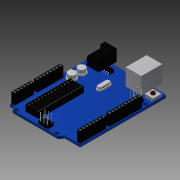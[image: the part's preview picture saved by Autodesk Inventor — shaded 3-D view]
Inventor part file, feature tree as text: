
AUTODESK INVENTOR PART (.ipt)
format: ipt  version: 2014 SP1 (Build 180222100, 222)  size: 1,044,992 bytes
history: native  units: mm
features: sketch x31, extrude x29, pattern_linear x9, revolve x5, fillet x2, plane x1, mirror x1
ambient origin geometry x8: Origin, YZ Plane, XZ Plane, XY Plane, X Axis, Y Axis, Z Axis, Center Point
bodies: Solid1 (feature_tree)
feature tree (78):
  extrude  "Extrusion1"  Depth=69.0mm
  extrude  "Extrusion2"  Depth=3.0mm
  sketch  "Sketch4"  dims[d10=3.0mm d11=5.0mm]
  extrude  "Extrusion3"  Depth=5.0mm
  pattern_linear  "Rectangular Pattern1"  Count1=6 Spacing1=2.5mm
  extrude  "Extrusion4"  Depth=2.5mm
  pattern_linear  "Rectangular Pattern2"  Count1=8 Spacing1=2.5mm
  sketch  "Sketch5"  dims[d13=3.0mm]
  extrude  "Extrusion5"  Depth=2.5mm
  pattern_linear  "Rectangular Pattern3"  Count1=8 Spacing1=2.5mm
  extrude  "Extrusion6"  Depth=2.5mm
  pattern_linear  "Rectangular Pattern4"  Count1=10 Spacing1=2.5mm
  sketch  "Sketch6"  dims[d15=21.587978mm]
  extrude  "Extrusion7"  Depth=35.0mm
  pattern_linear  "Rectangular Pattern5"  Spacing1=1.5mm  [1 undecoded]
  extrude  "Extrusion10"  Depth=2.5mm
  extrude  "Extrusion11"  Depth=1.25mm
  extrude  "Extrusion12"  Depth=1.5mm
  fillet  "Fillet1"  Radius=0.5mm
  extrude  "Extrusion13"  Depth=4.0mm TaperAngle=0.0deg
  pattern_linear  "Rectangular Pattern6"  Count1=14 Spacing1=2.5mm
  extrude  "Extrusion14"  Depth=4.0mm TaperAngle=0.0deg
  extrude  "Extrusion15"  Depth=1.0mm TaperAngle=0.0deg
  extrude  "Extrusion16"  Depth=2.5mm
  extrude  "Extrusion17"  Depth=5.0mm
  extrude  "Extrusion18"  Depth=0.5mm
  extrude  "Extrusion19"  Depth=24.0mm
  revolve  "Revolution1"  [1 undecoded]
  pattern_linear  "Rectangular Pattern7"  Spacing1=0.5mm  [1 undecoded]
  plane  "Work Plane1"
  mirror  "Mirror1"
  extrude  "Extrusion20"  Depth=0.5mm
  sketch  "Sketch21"  dims[d33=8.0mm d34=0.0mm d35=80.0mm d37=2.5mm]
  sketch  "Sketch22"  dims[d38=2.5mm d39=2.5mm]
  extrude  "Extrusion21"  Depth=0.5mm
  extrude  "Extrusion22"  Depth=3.5mm
  extrude  "Extrusion23"  Depth=2.0mm TaperAngle=0.0deg
  revolve  "Revolution2"  [1 undecoded]
  pattern_linear  "Rectangular Pattern8"  Spacing1=3.0mm  [1 undecoded]
  revolve  "Revolution3"  [1 undecoded]
  extrude  "Extrusion24"  Depth=2.5mm
  extrude  "Extrusion25"  Depth=3.0mm
  extrude  "Extrusion26"  Depth=2.0mm TaperAngle=0.0deg
  extrude  "Extrusion27"  Depth=13.999995mm
  revolve  "Revolution4"  [1 undecoded]
  revolve  "Revolution5"  [1 undecoded]
  extrude  "Extrusion28"  Depth=14.0mm
  extrude  "Extrusion29"  Depth=2.0mm
  extrude  "Extrusion30"  Depth=3.0mm
  fillet  "Fillet2"  Radius=14.0mm
  extrude  "Extrusion31"  Depth=2.0mm
  pattern_linear  "Rectangular Pattern9"  Spacing1=2.0mm  [1 undecoded]
  sketch  "Sketch1"  dims[d0=54.0mm d1=69.0mm]
  sketch  "Sketch3"  dims[d2=2.0mm d3=0.0mm d9=3.0mm]
  sketch  "Sketch9"  dims[d16=2.0mm d17=0.0mm]
  sketch  "Sketch10"  dims[d18=2.5mm]
  sketch  "Sketch11"  dims[d19=2.5mm]
  sketch  "Sketch12"  dims[d20=1.5mm]
  sketch  "Sketch13"  dims[d21=0.5mm]
  sketch  "Sketch14"  dims[d22=0.5mm]
  sketch  "Sketch15"  dims[d23=8.0mm d24=0.0mm d25=60.0mm d27=2.5mm]
  sketch  "Sketch16"  dims[d28=2.5mm d29=2.5mm]
  sketch  "Sketch17"  dims[d30=0.5mm]
  sketch  "Sketch19"  dims[d31=1.5mm]
  sketch  "Sketch20"  dims[d32=17.5mm]
  sketch  "Sketch23"  dims[d40=0.5mm]
  sketch  "Sketch24"  dims[d41=0.5mm]
  sketch  "Sketch25"  dims[d42=1.5mm]
  sketch  "Sketch26"  dims[d43=8.0mm d44=0.0mm d45=80.0mm d47=2.5mm]
  sketch  "Sketch27"  dims[d48=2.5mm d49=2.5mm]
  sketch  "Sketch28"  dims[d50=0.5mm]
  sketch  "Sketch29"  dims[d51=22.5mm]
  sketch  "Sketch30"  dims[d52=1.5mm]
  sketch  "Sketch31"  dims[d53=8.0mm d54=0.0mm d55=100.0mm d57=2.5mm]
  sketch  "Sketch32"  dims[d58=10.0mm d59=35.0mm]
  sketch  "Sketch33"  dims[d60=4.0mm]
  sketch  "Sketch34"  dims[d61=8.0mm]
  sketch  "Sketch35"  dims[d62=1.5mm d63=1.5mm d64=2.5mm d65=1.25mm d66=1.5mm d67=0.5mm d68=4.0mm d69=0.0mm d74=140.0mm d76=2.5mm d77=4.0mm d78=0.0mm d79=1.0mm d80=0.0mm d81=2.5mm d82=5.0mm d84=0.5mm d85=24.0mm d86=2.0mm d87=0.0mm d88=0.5mm d89=0.5mm d90=0.5mm d91=3.5mm d92=2.0mm d93=0.0mm d94=30.0mm d96=2.5mm d97=3.0mm d98=6.5mm d99=1.6mm d100=3.0mm d102=1.6mm d103=2.0mm d104=0.0mm d105=13.999995mm d106=6.0mm d107=3.0mm d108=14.0mm d109=2.0mm d110=3.0mm d111=14.0mm d112=2.0mm d113=2.0mm d114=0.0mm d115=12.0mm d116=16.0mm d117=6.0mm d118=9.0mm d119=13.0mm d120=0.0mm d121=1.0mm d122=2.0mm d123=2.5mm d124=6.0mm d125=6.0mm d126=3.0mm d127=2.0mm d128=7.0mm d129=0.0mm d130=6.5mm d131=6.5mm d132=3.0mm d133=0.5mm d134=2.0mm d135=0.0mm d136=3.0mm d137=1.0mm d138=0.0mm d142=90.0deg d143=30.0mm d145=2.0mm d146=-3.25mm d147=6.5mm d148=7.0mm d149=6.5mm d150=7.0mm d151=7.5mm d152=18.0mm d153=1.0mm d154=0.0mm d155=0.5mm d156=0.5mm d157=3.0mm d158=0.0mm d159=3.0mm d160=0.0mm d161=5.0mm d162=3.0mm d163=5.0mm d164=19.0mm d165=2.0mm d166=0.0mm d167=0.5mm d168=1.0mm d169=4.0mm d170=90.0deg d171=30.0mm d173=1.5mm d174=0.5mm d175=0.5mm d176=1.0mm d177=3.0mm d178=90.0deg d179=9.0mm d180=3.5mm d181=0.5mm d182=4.0mm d183=9.0mm d184=0.0mm d185=10.5mm d186=0.0mm d188=6.0mm d189=8.0mm d190=0.0mm d191=2.0mm d192=3.5mm d193=1.0mm d194=20.0mm d195=1.0mm d196=0.0mm d197=0.5mm d198=90.0deg d199=0.5mm d200=90.0deg d201=4.0mm d202=6.0mm d203=16.0mm d204=25.0mm d205=1.0mm d206=0.0mm d207=0.5mm d208=1.5mm d209=0.0mm d210=5.0mm d211=2.5mm d212=13.0mm d213=4.0mm d214=2.0mm d215=0.0mm d216=0.5mm d217=0.5mm d218=0.5mm d219=3.5mm d220=6.0mm d221=0.0mm d222=30.0mm d224=2.5mm]
note: 9 required parameter values undecoded (feature->parameter linkage not recoverable at this tier; creation-order binding heuristic only, values carry confidence <= 0.55)